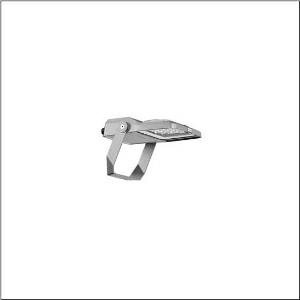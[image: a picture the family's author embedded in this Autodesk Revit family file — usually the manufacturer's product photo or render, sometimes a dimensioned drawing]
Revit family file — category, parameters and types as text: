
# Revit family: floodlight_fl_21_iq_micro___rs12_5xa7762a1b1a_c11c
name_source: partatom
category: Lighting Fixtures
units: mm (PartAtom-declared; Revit-internal decimal feet)

## family parameters
Cut with Voids When Loaded = No
Host = Face
Light Source = No
Part Type = Normal
Room Calculation Point = No
Round Connector Dimension = Use Diameter
Shared = No

## types (1)
- --- (1 x LED, 2560 lm, 23.1 W, 2200K)
    Apparent Load = 23 VA
    CIE Flux Codes = 79 92 99 100 100
    Color Rendering = 70
    Color Temperature = 2200K
    Default Elevation = 1800 mm
    Description = Floodlight FL 21 iQ micro, floodlight, primary light control with lens, of PMMA, primary optical cover: protective disc, of toughened safety glass, transparent, light distribution: RS12, light emission: direct distribution, installation type: surface-mounted, LED, High Power LED, rated luminous flux: 2.560lm, luminous efficacy: 111lm/W, light colour: 722, colour temperature: 2200K, control gear: iQ Street-Remote/DALI, control: Auto-Match, Temp-Guard, Night-Set, Smart-Wire, Desk-Remote (wireless, voltage-free reading and setting of iQ features in the workshop via application-optimized NFC function/RFID function), optimised constant luminous flux control (CLO 2.0), Street-Remote, with terminal, 6-pole, mains connection: 220..240V, AC, 50/60Hz, start of lifetime: 23W, end of service life: 24W, reduction: 11W, luminaire housing, of diecast aluminium, powder-coated, Siteco® metallic grey (DB 702S), corrosivity category C5 mid according to DIN EN ISO 12944, suitable for swimming pools, chlorine-resistant, sealing non-destructively replaceable, mounting bracket, of steel, galvanised, powder-coated, Siteco® metallic grey (DB 702S), protection rating (complete): IP66, insulation class (complete): insulation class II (safety insulation), certification: CE, ENEC, VDE, protection symbol: D, impact resistance: IK07, permissible operating ambient temperature: -40..+40°C, permissible operating ambient temperature for outdoor applications: -40..+50°C, standard: DIN EN 12944, LABS conformity tested according to VDMA 24364:2018-05, packaging unit: 1 piece

Light Distribution: RS12
    Height = 65 mm
    Lamp = 1 x LED
    Lamp Light Flux = 2560 lm
    Lamp Power = 23.1 W
    Lamp count = 1
    Length = 312 mm
    Luminous efficacy = 111 lm/W
    Manufacturer = Siteco
    ModVariant = No
    Model = 5XA7762A1B1A
    Number of Poles = 1
    OnlyDefault = Yes
    Power Factor = 1
    Product Name = Floodlight FL 21 iQ micro | RS12
    Product group = floodlight | pylon annexe
    ProductGroupID = 6200
    Protection Class = Protection class II
    Protection Degree = IP 66
    RLX_Detail_Level = 1
    RLX_Emergency_Light_Flux = 0 lm
    RLX_Emergency_Type = 0
    RLX_Emergency_Type_DB = No
    RlxData = <blob elided: 75177 chars, md5=8edb88a3>
    Socket = socket
    Standby Power = 0 W
    System Light Flux = 2560 lm
    System Power = 23 W
    Type Comments = factory setting: luminous flux: 100 % | dim-lin: 254 | 455 mA
    Type Image = l_1006880.jpg
    URL = http://relux.com
    VarID = @adj_181858
    Voltage = 0 V
    Weight = 0.00 kg
    Width = 230 mm

## geometry (parser evidence)
native form markers: Blend x4, Sweep x13
no freeform markers — native parametric forms only
